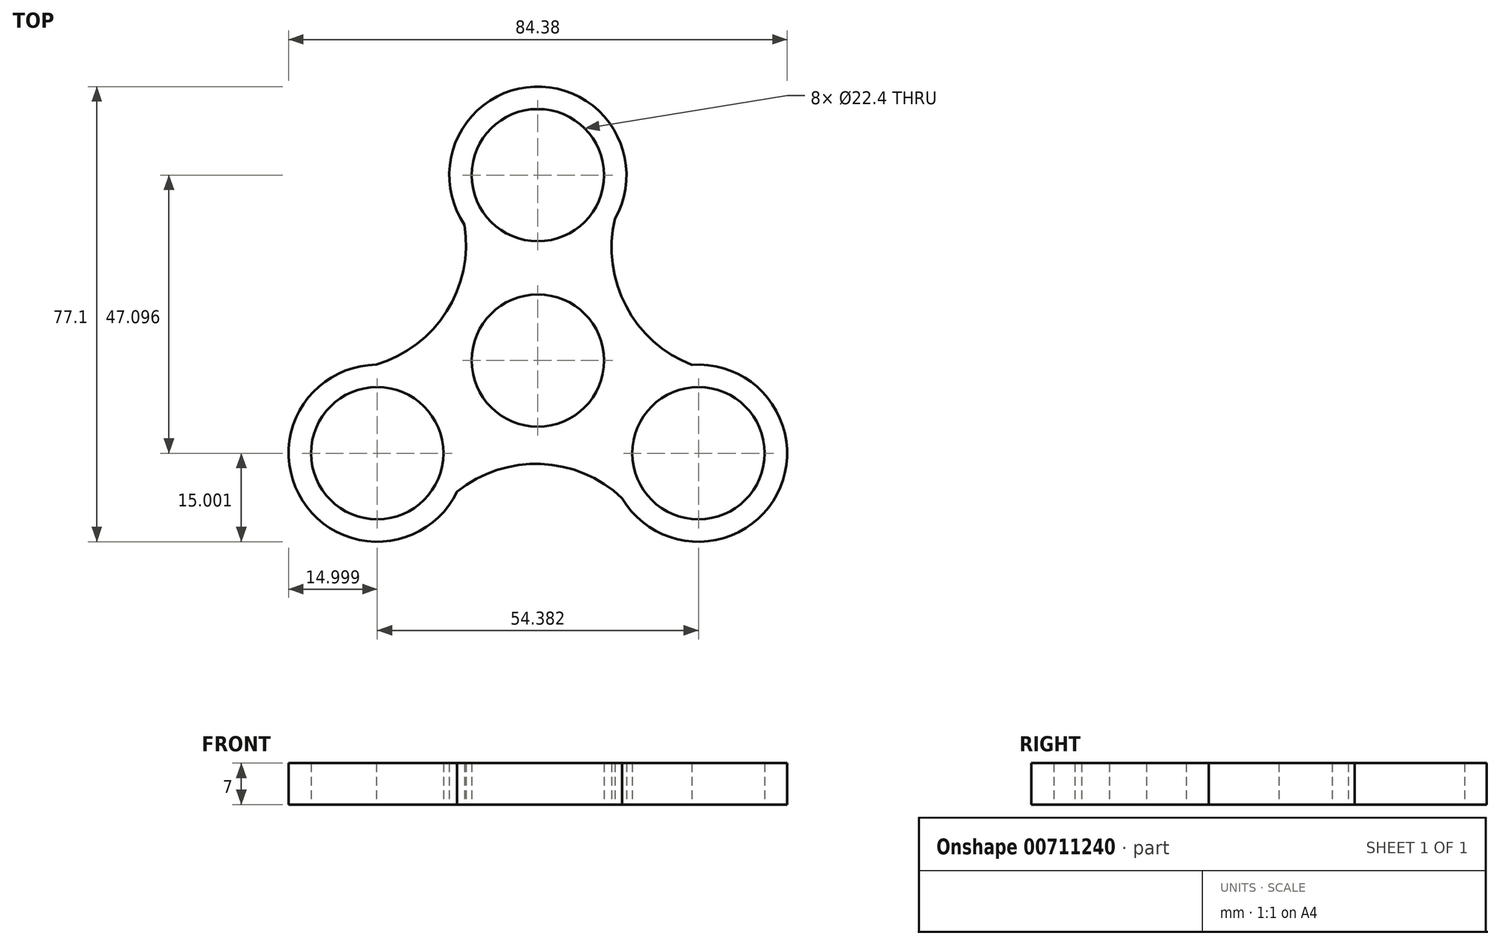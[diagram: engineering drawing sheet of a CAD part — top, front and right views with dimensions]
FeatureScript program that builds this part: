
annotation { "Feature Type Name" : "Feature", "Feature Type Description" : "" }
export const myFeature = defineFeature(function(context is Context, id is Id, definition is map)
    precondition{}
    {
        {
            var Q0;
            Q0=qCreatedBy(makeId("Top.planeOp"),FACE);
            var sketch = newSketch(context, id + "F0", { "sketchPlane" : qUnion([Q0])});
            skCircle(sketch, "E0", {"center": v(0, 0) * mm, "radius": 11.2 * mm});
            skArc(sketch, "E1", {"start": v(13.07, 24.03) * mm, "mid": v(-0.63, 46.38) * mm, "end": v(-12.4, 22.97) * mm});
            skCircle(sketch, "E2", {"center": v(0, 31.4) * mm, "radius": 11.2 * mm});
            skCircle(sketch, "E3.1.0", {"center": v(-27.2, -15.7) * mm, "radius": 11.2 * mm});
            skArc(sketch, "E3.1.1", {"start": v(-27.35, -0.7) * mm, "mid": v(-39.86, -23.73) * mm, "end": v(-13.69, -22.23) * mm});
            skCircle(sketch, "E3.2.0", {"center": v(27.2, -15.7) * mm, "radius": 11.2 * mm});
            skArc(sketch, "E3.2.1", {"start": v(14.28, -23.34) * mm, "mid": v(40.48, -22.65) * mm, "end": v(26.1, -0.74) * mm});
            skArc(sketch, "E4", {"start": v(13.07, 24.03) * mm, "mid": v(14.93, 9.2) * mm, "end": v(26.1, -0.74) * mm});
            skArc(sketch, "E5.1.0", {"start": v(-27.35, -0.7) * mm, "mid": v(-15.43, 8.33) * mm, "end": v(-12.4, 22.97) * mm});
            skArc(sketch, "E5.2.0", {"start": v(14.28, -23.34) * mm, "mid": v(0.5, -17.53) * mm, "end": v(-13.69, -22.23) * mm});
            skSolve(sketch);
        }
        {
            var Q0;
            Q0=makeQuery(id+"F0.imprint","IMPRINT",FACE,{"disambiguationData":[TD([[makeQuery(id+"F0.imprint","IMPRINT",EDGE,{"derivedFrom":sQuery(id+"F0.wireOp",EDGE,"E0")}),-1.0]])]});
            extrude(context, id + "F1", {"entities" : qUnion([Q0]), "depth" : 7 * mm, "offsetDistance" : 25 * mm});
        }
    });
